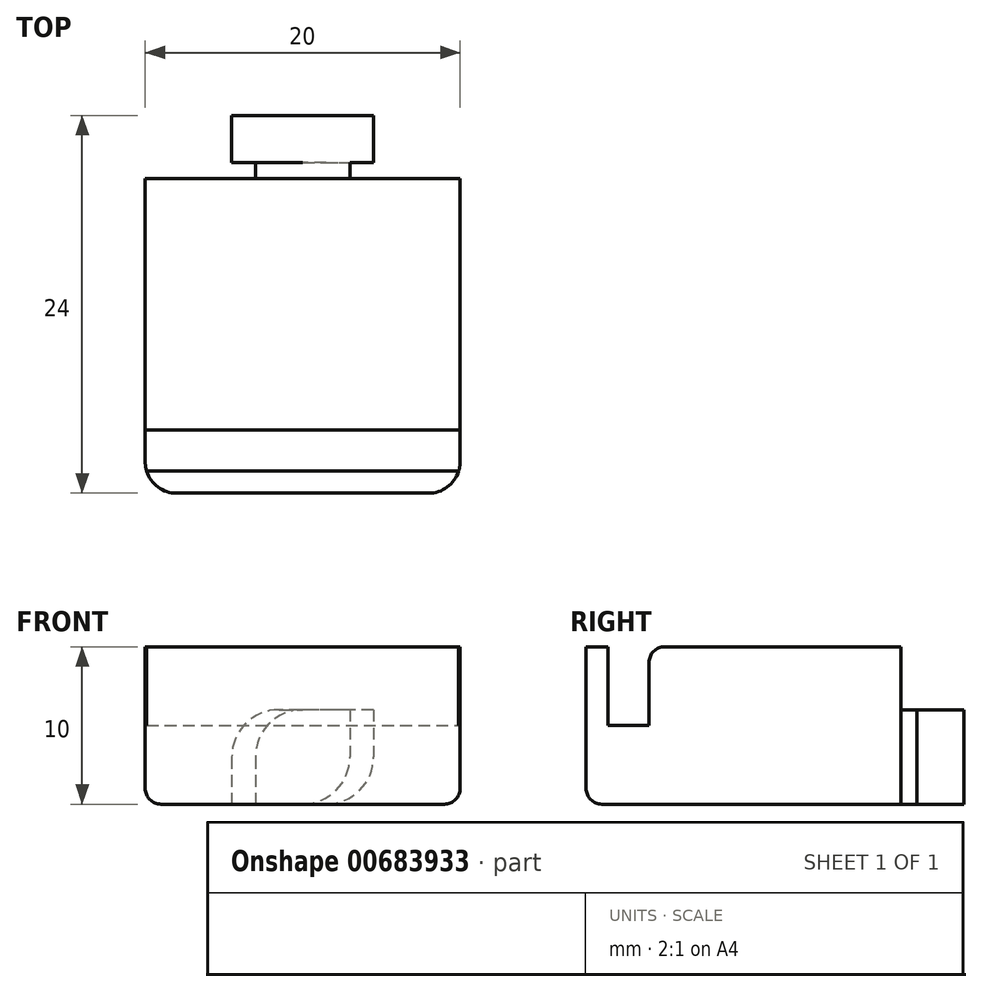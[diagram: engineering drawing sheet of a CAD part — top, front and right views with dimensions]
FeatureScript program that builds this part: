
annotation { "Feature Type Name" : "Feature", "Feature Type Description" : "" }
export const myFeature = defineFeature(function(context is Context, id is Id, definition is map)
    precondition{}
    {
        {
            var Q0;
            Q0=qCreatedBy(makeId("Top.planeOp"),FACE);
            var sketch = newSketch(context, id + "F0", { "sketchPlane" : qUnion([Q0])});
            skLineSegment(sketch, "E0", {"start": v(0, 4) * mm, "end": v(4.5, 4) * mm});
            skLineSegment(sketch, "E1", {"start": v(4.5, 4) * mm, "end": v(4.5, 1) * mm});
            skLineSegment(sketch, "E2", {"start": v(4.5, 1) * mm, "end": v(3, 1) * mm});
            skLineSegment(sketch, "E3", {"start": v(3, 1) * mm, "end": v(3, 0) * mm});
            skLineSegment(sketch, "E4", {"start": v(3, 0) * mm, "end": v(4.5, 0) * mm});
            skLineSegment(sketch, "E5.MirrorCS", {"start": v(-3, 1) * mm, "end": v(-3, 0) * mm});
            skLineSegment(sketch, "E6.MirrorCS", {"start": v(-4.5, 1) * mm, "end": v(-3, 1) * mm});
            skLineSegment(sketch, "E7.MirrorCS", {"start": v(-3, 0) * mm, "end": v(-4.5, 0) * mm});
            skLineSegment(sketch, "E8.MirrorCS", {"start": v(0, 4) * mm, "end": v(-4.5, 4) * mm});
            skLineSegment(sketch, "E9.MirrorCS", {"start": v(-4.5, 4) * mm, "end": v(-4.5, 1) * mm});
            skLineSegment(sketch, "E10", {"start": v(4.5, 0) * mm, "end": v(10, 0) * mm});
            skLineSegment(sketch, "E11", {"start": v(10, 0) * mm, "end": v(10, -20) * mm});
            skLineSegment(sketch, "E12", {"start": v(10, -20) * mm, "end": v(0, -20) * mm});
            skLineSegment(sketch, "E13.MirrorCS", {"start": v(-10, -20) * mm, "end": v(0, -20) * mm});
            skLineSegment(sketch, "E14.MirrorCS", {"start": v(-10, 0) * mm, "end": v(-10, -20) * mm});
            skLineSegment(sketch, "E15.MirrorCS", {"start": v(-4.5, 0) * mm, "end": v(-10, 0) * mm});
            skSolve(sketch);
        }
        {
            var Q0;
            Q0 = qSketchRegion(id + "F0", true);
            extrude(context, id + "F1", {"entities" : qUnion([Q0]), "depth" : 10 * mm, "offsetDistance" : 25 * mm});
        }
        {
            var Q0;
            Q0=makeQuery(id+"F1.opExtrude","SWEPT_FACE",FACE,{"disambiguationData":[OSD([sQuery(id+"F0.wireOp",EDGE,"E14.MirrorCS")])]});
            var sketch = newSketch(context, id + "F2", { "sketchPlane" : qUnion([Q0])});
            skLineSegment(sketch, "E16", {"start": v(0, 6) * mm, "end": v(-4.58, 6) * mm});
            skLineSegment(sketch, "E17", {"start": v(-4.58, 6) * mm, "end": v(-4.58, 10) * mm});
            skLineSegment(sketch, "E18", {"start": v(-4.58, 10) * mm, "end": v(0, 10) * mm});
            skLineSegment(sketch, "E19", {"start": v(0, 10) * mm, "end": v(0, 6) * mm});
            skSolve(sketch);
        }
        {
            var Q0;
            Q0 = qSketchRegion(id + "F2", true);
            extrude(context, id + "F3", {"entities" : qUnion([Q0]), "operationType" : NewBodyOperationType.REMOVE, "oppositeDirection" : true, "depth" : 25 * mm, "offsetDistance" : 25 * mm});
        }
        {
            var Q0;
            Q0=makeQuery(id+"F1.opExtrude","SWEPT_FACE",FACE,{"disambiguationData":[OSD([sQuery(id+"F0.wireOp",EDGE,"E11")])]});
            var sketch = newSketch(context, id + "F4", { "sketchPlane" : qUnion([Q0])});
            skLineSegment(sketch, "E20", {"start": v(-18.6, 10) * mm, "end": v(-18.6, 5) * mm});
            skLineSegment(sketch, "E21", {"start": v(-18.6, 5) * mm, "end": v(-16, 5) * mm});
            skLineSegment(sketch, "E22", {"start": v(-16, 5) * mm, "end": v(-16, 10) * mm});
            skLineSegment(sketch, "E23", {"start": v(-18.6, 10) * mm, "end": v(-16, 10) * mm});
            skSolve(sketch);
        }
        {
            var Q0;
            Q0 = qSketchRegion(id + "F4", true);
            extrude(context, id + "F5", {"entities" : qUnion([Q0]), "operationType" : NewBodyOperationType.REMOVE, "oppositeDirection" : true, "depth" : 25 * mm, "offsetDistance" : 25 * mm});
        }
        {
            var Q0;
            Q0=makeQuery(id+"F1.opExtrude","CAP_EDGE",EDGE,{"disambiguationData":[OSD([sQuery(id+"F0.wireOp",EDGE,"E3")])],"isStart":true});
            var Q1;
            Q1=makeQuery(id+"F3.boolean.opBoolean","INTERSECT",EDGE,{"derivedFrom":[makeQuery(id+"F1.opExtrude","SWEPT_FACE",FACE,{"disambiguationData":[OSD([sQuery(id+"F0.wireOp",EDGE,"E5.MirrorCS")])]}),makeQuery(id+"F3.opExtrude","SWEPT_FACE",FACE,{"disambiguationData":[OSD([sQuery(id+"F2.wireOp",EDGE,"E16")])]})]});
            fillet(context, id + "F6", {"entities" : qUnion([Q0, Q1]), "radius" : 3 * mm, "tangentPropagation" : true, "allowEdgeOverflow" : false});
        }
        {
            var Q0;
            Q0=makeQuery(id+"F1.opExtrude","CAP_EDGE",EDGE,{"disambiguationData":[OSD([sQuery(id+"F0.wireOp",EDGE,"E1")])],"isStart":true});
            var Q1;
            Q1=makeQuery(id+"F3.boolean.opBoolean","INTERSECT",EDGE,{"derivedFrom":[makeQuery(id+"F1.opExtrude","SWEPT_FACE",FACE,{"disambiguationData":[OSD([sQuery(id+"F0.wireOp",EDGE,"E9.MirrorCS")])]}),makeQuery(id+"F3.opExtrude","SWEPT_FACE",FACE,{"disambiguationData":[OSD([sQuery(id+"F2.wireOp",EDGE,"E16")])]})]});
            fillet(context, id + "F7", {"entities" : qUnion([Q0, Q1]), "radius" : 3 * mm, "tangentPropagation" : true, "allowEdgeOverflow" : false});
        }
        {
            var Q0;
            {var subQ0=sQuery(id+"F0.wireOp",EDGE,"E14.MirrorCS");Q0=makeQuery(id+"F5.boolean.opBoolean","SPLIT",EDGE,{"disambiguationData":[TD([makeQuery(id+"F3.opExtrude","SWEPT_FACE",FACE,{"disambiguationData":[OSD([sQuery(id+"F2.wireOp",EDGE,"E19")])]})])],"derivedFrom":makeQuery(id+"F1.opExtrude","CAP_EDGE",EDGE,{"disambiguationData":[OSD([subQ0])],"isStart":false})});}
            var Q1;
            {var subQ2=sQuery(id+"F0.wireOp",EDGE,"E11");Q1=makeQuery(id+"F5.boolean.opBoolean","SPLIT",EDGE,{"disambiguationData":[TD([makeQuery(id+"F3.opExtrude","SWEPT_FACE",FACE,{"disambiguationData":[OSD([sQuery(id+"F2.wireOp",EDGE,"E19")])]})])],"derivedFrom":makeQuery(id+"F1.opExtrude","CAP_EDGE",EDGE,{"disambiguationData":[OSD([subQ2])],"isStart":false})});}
            var Q2;
            Q2=makeQuery(id+"F1.opExtrude","CAP_EDGE",EDGE,{"disambiguationData":[OSD([sQuery(id+"F0.wireOp",EDGE,"E14.MirrorCS")])],"isStart":true});
            var Q3;
            Q3=makeQuery(id+"F1.opExtrude","CAP_EDGE",EDGE,{"disambiguationData":[OSD([sQuery(id+"F0.wireOp",EDGE,"E12"),sQuery(id+"F0.wireOp",EDGE,"E13.MirrorCS")])],"isStart":true});
            var Q4;
            Q4=makeQuery(id+"F1.opExtrude","CAP_EDGE",EDGE,{"disambiguationData":[OSD([sQuery(id+"F0.wireOp",EDGE,"E11")])],"isStart":true});
            var Q5;
            Q5=makeQuery(id+"F5.boolean.opBoolean","COPY",EDGE,{"derivedFrom":makeQuery(id+"F5.opExtrude","SWEPT_EDGE",EDGE,{"disambiguationData":[OSD([sQuery(id+"F0.wireOp",EDGE,"E11"),sQuery(id+"F4.wireOp",EDGE,"E20"),sQuery(id+"F4.wireOp",EDGE,"E23")])]})});
            var Q6;
            Q6=makeQuery(id+"F5.boolean.opBoolean","COPY",EDGE,{"derivedFrom":makeQuery(id+"F5.opExtrude","SWEPT_EDGE",EDGE,{"disambiguationData":[OSD([sQuery(id+"F0.wireOp",EDGE,"E11"),sQuery(id+"F4.wireOp",EDGE,"E22"),sQuery(id+"F4.wireOp",EDGE,"E23")])]})});
            fillet(context, id + "F8", {"entities" : qUnion([Q0, Q1, Q2, Q3, Q4, Q5, Q6]), "radius" : 1 * mm, "tangentPropagation" : true, "allowEdgeOverflow" : false});
        }
        {
            var Q0;
            Q0=makeQuery(id+"F1.opExtrude","SWEPT_EDGE",EDGE,{"disambiguationData":[OSD([sQuery(id+"F0.wireOp",EDGE,"E11"),sQuery(id+"F0.wireOp",EDGE,"E12")])]});
            var Q1;
            Q1=makeQuery(id+"F1.opExtrude","SWEPT_EDGE",EDGE,{"disambiguationData":[OSD([sQuery(id+"F0.wireOp",EDGE,"E13.MirrorCS"),sQuery(id+"F0.wireOp",EDGE,"E14.MirrorCS")])]});
            fillet(context, id + "F9", {"entities" : qUnion([Q0, Q1]), "radius" : 2 * mm, "tangentPropagation" : true, "allowEdgeOverflow" : false});
        }
    });
